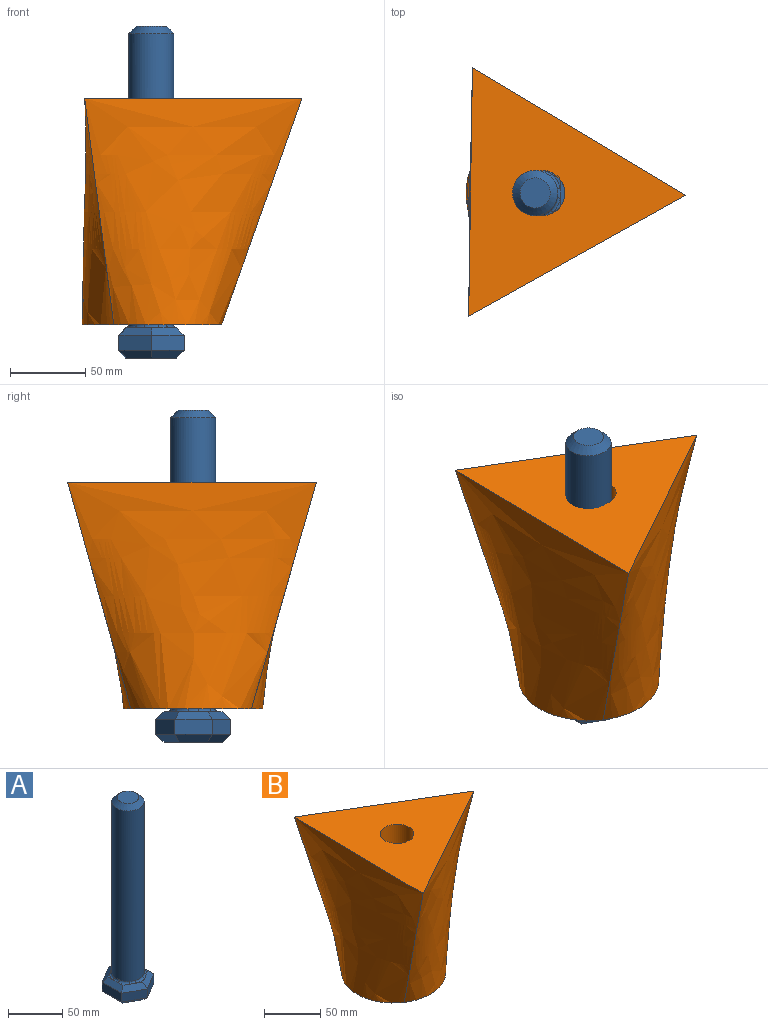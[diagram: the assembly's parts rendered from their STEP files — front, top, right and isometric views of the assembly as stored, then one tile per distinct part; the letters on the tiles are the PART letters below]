
ASSEMBLY  parts=2 mates=1
PART A: 40 faces, bbox 43.8x50x220 mm
  f0: plane 9.37x5.3mm, normal (0,0,1), area 10.3mm2, adj f15,f16,f37
  f1: plane 10.71x3.19mm, normal (0,0,1), area 10.3mm2, adj f16,f18,f33
  f2: plane 9.18x5.52mm, normal (0,0,1), area 10.3mm2, adj f18,f20,f29
  f3: plane 9.37x5.3mm, normal (0,0,1), area 10.3mm2, adj f19,f20,f30
  f4: plane 10.71x3.19mm, normal (0,0,1), area 10.3mm2, adj f17,f19,f34
  f5: plane 25x10mm, normal (1,0.02,0), area 250mm2, adj f6,f10,f15,f25
  f6: plane 21.87x12.12mm, normal (0.48,0.87,0), area 250mm2, adj f5,f7,f17,f26
  f7: plane 21.43x12.88mm, normal (-0.52,0.86,0), area 250mm2, adj f6,f8,f19,f24
  f8: plane 25x10mm, normal (-1,-0.02,0), area 250mm2, adj f7,f9,f20,f22
  f9: plane 21.87x12.12mm, normal (-0.48,-0.87,0), area 250mm2, adj f8,f10,f18,f21
  f10: plane 21.43x12.88mm, normal (0.52,-0.86,0), area 250mm2, adj f5,f9,f16,f23
  f11: plane 9.18x5.52mm, normal (0,0,1), area 10.3mm2, adj f15,f17,f38
  f12: plane 38.45x33.63mm, normal (0,0,-1), area 960.4mm2, adj f21,f22,f23,f24,f25,f26
  f13: cylinder r=15mm len=193mm, axis (0,0,-1), area 18189.8mm2, adj f27,f28,f29,f30,f31,f32,f33,f34
  f14: plane 20x20mm, normal (0,0,1), area 314.2mm2, adj f27
  f15: plane 25.03x5.42mm, normal (0.71,0.01,0.71), area 156.4mm2, adj f0,f5,f11,f16,f17,f39
  f16: plane 21.56x15.7mm, normal (0.36,-0.61,0.71), area 156.4mm2, adj f0,f1,f10,f15,f18,f35
  f17: plane 21.9x15.12mm, normal (0.34,0.62,0.71), area 156.4mm2, adj f4,f6,f11,f15,f19,f36
  f18: plane 21.9x15.12mm, normal (-0.34,-0.62,0.71), area 156.4mm2, adj f1,f2,f9,f16,f20,f31
  f19: plane 21.56x15.7mm, normal (-0.36,0.61,0.71), area 156.4mm2, adj f3,f4,f7,f17,f20,f32
  f20: plane 25.03x5.42mm, normal (-0.71,-0.01,0.71), area 156.4mm2, adj f2,f3,f8,f18,f19,f28
  f21: plane 21.87x15.09mm, normal (-0.34,-0.62,-0.71), area 156.4mm2, adj f9,f12,f22,f23
  f22: plane 25x5.39mm, normal (-0.71,-0.01,-0.71), area 156.4mm2, adj f8,f12,f21,f24
  f23: plane 21.53x15.68mm, normal (0.36,-0.61,-0.71), area 156.4mm2, adj f10,f12,f21,f25
  f24: plane 21.53x15.68mm, normal (-0.36,0.61,-0.71), area 156.4mm2, adj f7,f12,f22,f26
  f25: plane 25x5.39mm, normal (0.71,0.01,-0.71), area 156.4mm2, adj f5,f12,f23,f26
  f26: plane 21.87x15.09mm, normal (0.34,0.62,-0.71), area 156.4mm2, adj f6,f12,f24,f25
  f27: cone r=10mm half-angle=45deg, axis (0,0,-1), area 555.4mm2, adj f13,f14
  f28: bspline ~9.27x2.39mm, area 18.5mm2, adj f13,f20,f29,f30
  f29: torus R=17mm, axis (0,0,1), area 31.7mm2, adj f2,f13,f28,f31
  f30: torus R=17mm, axis (0,0,1), area 31.7mm2, adj f3,f13,f28,f32
  f31: bspline ~8.71x6.15mm, area 18.5mm2, adj f13,f18,f29,f33
  f32: bspline ~6.54x5mm, area 18.5mm2, adj f13,f19,f30,f34
  f33: torus R=17mm, axis (0,0,1), area 31.7mm2, adj f1,f13,f31,f35
  f34: torus R=17mm, axis (0,0,1), area 31.7mm2, adj f4,f13,f32,f36
  f35: bspline ~6.54x5mm, area 18.5mm2, adj f13,f16,f33,f37
  f36: bspline ~8.71x6.15mm, area 18.5mm2, adj f13,f17,f34,f38
  f37: torus R=17mm, axis (0,0,1), area 31.7mm2, adj f0,f13,f35,f39
  f38: torus R=17mm, axis (0,0,1), area 31.7mm2, adj f11,f13,f36,f39
  f39: bspline ~9.27x2.39mm, area 18.5mm2, adj f13,f15,f37,f38
PART B: 6 faces, bbox 145.8x164.8x150 mm
  f0: plane 92.62x92.62mm, normal (0,0,-1), area 6019.7mm2, adj f2,f3,f4,f5
  f1: plane 164.78x143.95mm, normal (0,0,1), area 11052.6mm2, adj f2,f3,f4,f5
  f2: bspline ~164.78x150mm, area 19162.7mm2, adj f0,f1,f3,f4
  f3: bspline ~150x143.95mm, area 19221.1mm2, adj f0,f1,f2,f4
  f4: bspline ~150x141.45mm, area 19224.5mm2, adj f0,f1,f2,f3
  f5: cylinder r=15mm len=150mm, axis (0,0,-1), area 14137.2mm2, adj f0,f1
PLACE A t=(21.9,70.57,-32.46)mm
PLACE B t=(26.67,70.57,-10.46)mm
MATE fastened A.f13 <-> B.f0  axis (0,0,1) through (21.9,70.57,-10.46)mm
